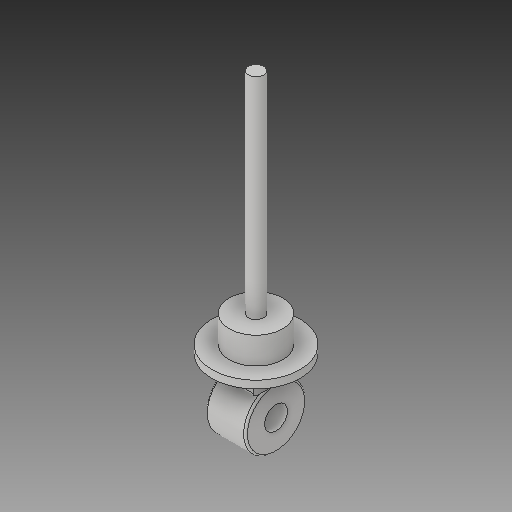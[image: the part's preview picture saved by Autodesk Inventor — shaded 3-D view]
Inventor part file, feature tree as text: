
AUTODESK INVENTOR PART (.ipt)
format: ipt  version: 2018 (Build 220112000, 112)  size: 172,544 bytes
history: native  units: mm
features: sketch x5, extrude x4, fillet x4, other x2, hole x1
ambient origin geometry x8: Origin, YZ Plane, XZ Plane, XY Plane, X Axis, Y Axis, Z Axis, Center Point
bodies: Body1 (feature_tree)
feature tree (16):
  other  "ソリッド1"
  extrude  "押し出し1"  Depth=32.0mm
  hole  "穴1"  [1 undecoded]
  other  "作業平面1"
  extrude  "押し出し2"  Depth=24.0mm
  extrude  "押し出し3"  Depth=46.0mm
  extrude  "押し出し4"  Depth=4.0mm TaperAngle=0.0deg
  fillet  "フィレット1"  Radius=28.0mm
  fillet  "フィレット2"  Radius=14.0mm
  fillet  "フィレット3"  Radius=8.0mm
  fillet  "フィレット4"  Radius=110.0mm
  sketch  "スケッチ1"
  sketch  "スケッチ2"
  sketch  "スケッチ4"
  sketch  "スケッチ5"
  sketch  "スケッチ6"
note: 1 required parameter value undecoded (feature->parameter linkage not recoverable at this tier; creation-order binding heuristic only, values carry confidence <= 0.55)
